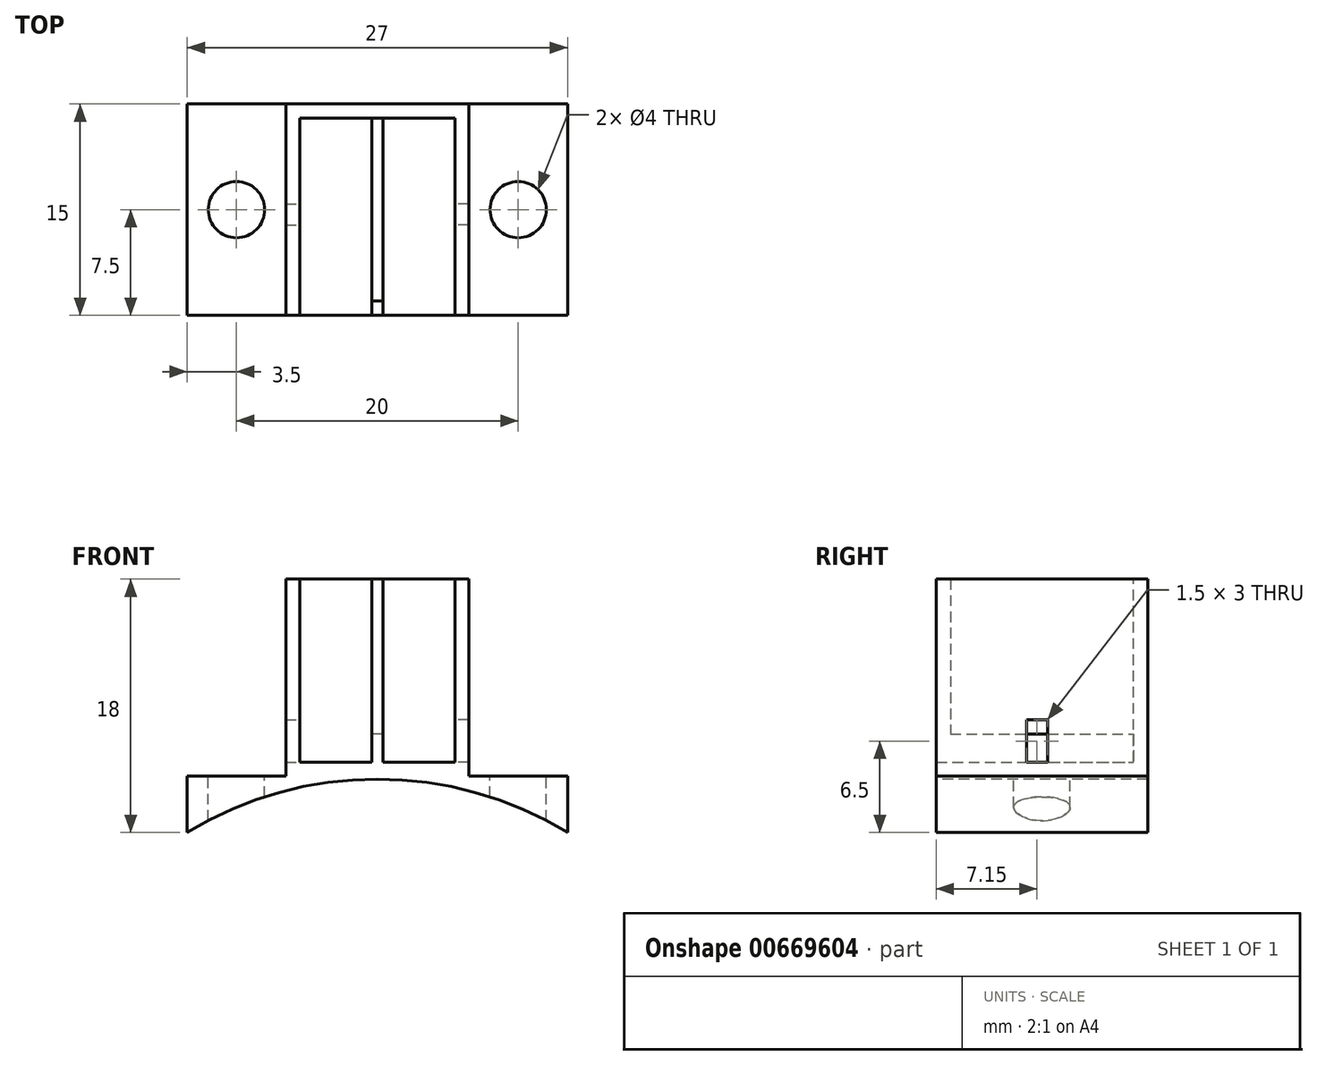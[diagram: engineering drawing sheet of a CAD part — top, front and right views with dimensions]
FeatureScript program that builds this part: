
annotation { "Feature Type Name" : "Feature", "Feature Type Description" : "" }
export const myFeature = defineFeature(function(context is Context, id is Id, definition is map)
    precondition{}
    {
        {
            var Q0;
            Q0=qCreatedBy(makeId("Top.planeOp"),FACE);
            var sketch = newSketch(context, id + "F0", { "sketchPlane" : qUnion([Q0])});
            skLineSegment(sketch, "E0.bottom", {"start": v(5.5, -6.5) * mm, "end": v(-5.5, -6.5) * mm});
            skLineSegment(sketch, "E0.top", {"start": v(5.5, 6.5) * mm, "end": v(-5.5, 6.5) * mm});
            skLineSegment(sketch, "E0.left", {"start": v(5.5, -6.5) * mm, "end": v(5.5, 6.5) * mm});
            skLineSegment(sketch, "E0.right", {"start": v(-5.5, -6.5) * mm, "end": v(-5.5, 6.5) * mm});
            skPoint(sketch, "E0.middle", {"position": v(0, 0) * mm});
            skSolve(sketch);
        }
        {
            var Q0;
            Q0=qCreatedBy(makeId("Top.planeOp"),FACE);
            var sketch = newSketch(context, id + "F1", { "sketchPlane" : qUnion([Q0])});
            skLineSegment(sketch, "E1.bottom", {"start": v(6.5, -7.5) * mm, "end": v(-6.5, -7.5) * mm});
            skLineSegment(sketch, "E1.top", {"start": v(6.5, 7.5) * mm, "end": v(-6.5, 7.5) * mm});
            skLineSegment(sketch, "E1.left", {"start": v(6.5, -7.5) * mm, "end": v(6.5, 7.5) * mm});
            skLineSegment(sketch, "E1.right", {"start": v(-6.5, -7.5) * mm, "end": v(-6.5, 7.5) * mm});
            skPoint(sketch, "E1.middle", {"position": v(0, 0) * mm});
            skSolve(sketch);
        }
        {
            var Q0;
            Q0 = qSketchRegion(id + "F1", true);
            extrude(context, id + "F2", {"entities" : qUnion([Q0]), "oppositeDirection" : true, "depth" : 18 * mm, "offsetDistance" : 25 * mm});
        }
        {
            var Q0;
            Q0 = qSketchRegion(id + "F0", true);
            extrude(context, id + "F3", {"entities" : qUnion([Q0]), "operationType" : NewBodyOperationType.REMOVE, "oppositeDirection" : true, "depth" : 13 * mm, "offsetDistance" : 25 * mm});
        }
        {
            var Q0;
            Q0=makeQuery(id+"F3.boolean.opBoolean","COPY",FACE,{"derivedFrom":makeQuery(id+"F3.opExtrude","CAP_FACE",FACE,{"disambiguationData":[OSD([sQuery(id+"F0.wireOp",EDGE,"E0.bottom"),sQuery(id+"F0.wireOp",EDGE,"E0.top"),sQuery(id+"F0.wireOp",EDGE,"E0.left"),sQuery(id+"F0.wireOp",EDGE,"E0.right")])],"isStart":false})});
            var sketch = newSketch(context, id + "F4", { "sketchPlane" : qUnion([Q0])});
            skLineSegment(sketch, "E2.bottom", {"start": v(0.4, -6.5) * mm, "end": v(-0.4, -6.5) * mm});
            skLineSegment(sketch, "E2.top", {"start": v(0.4, 6.5) * mm, "end": v(-0.4, 6.5) * mm});
            skLineSegment(sketch, "E2.left", {"start": v(0.4, -6.5) * mm, "end": v(0.4, 6.5) * mm});
            skLineSegment(sketch, "E2.right", {"start": v(-0.4, -6.5) * mm, "end": v(-0.4, 6.5) * mm});
            skPoint(sketch, "E2.middle", {"position": v(0, 0) * mm});
            skSolve(sketch);
        }
        {
            var Q0;
            Q0 = qSketchRegion(id + "F4", true);
            extrude(context, id + "F5", {"entities" : qUnion([Q0]), "operationType" : NewBodyOperationType.ADD, "depth" : 2 * mm, "offsetDistance" : 25 * mm});
        }
        {
            var Q0;
            {var subQ0=sQuery(id+"F0.wireOp",EDGE,"E0.bottom");var subQ1=sQuery(id+"F0.wireOp",EDGE,"E0.top");var subQ2=sQuery(id+"F0.wireOp",EDGE,"E0.left");Q0=makeQuery(id+"F5.boolean.opBoolean","SPLIT",FACE,{"disambiguationData":[TD([makeQuery(id+"F3.boolean.opBoolean","COPY",FACE,{"derivedFrom":makeQuery(id+"F3.opExtrude","SWEPT_FACE",FACE,{"disambiguationData":[OSD([subQ2])]})})])],"derivedFrom":makeQuery(id+"F3.boolean.opBoolean","COPY",FACE,{"derivedFrom":makeQuery(id+"F3.opExtrude","CAP_FACE",FACE,{"disambiguationData":[OSD([subQ0,subQ1,subQ2,sQuery(id+"F0.wireOp",EDGE,"E0.right")])],"isStart":false})})});}
            var sketch = newSketch(context, id + "F6", { "sketchPlane" : qUnion([Q0])});
            skLineSegment(sketch, "E3.bottom", {"start": v(0.4, -5.5) * mm, "end": v(5.5, -5.5) * mm});
            skLineSegment(sketch, "E3.top", {"start": v(0.4, -8.23) * mm, "end": v(5.5, -8.23) * mm});
            skLineSegment(sketch, "E3.left", {"start": v(0.4, -5.5) * mm, "end": v(0.4, -8.23) * mm});
            skLineSegment(sketch, "E3.right", {"start": v(5.5, -5.5) * mm, "end": v(5.5, -8.23) * mm});
            skSolve(sketch);
        }
        {
            var Q0;
            {var subQ0=sQuery(id+"F0.wireOp",EDGE,"E0.bottom");var subQ1=sQuery(id+"F0.wireOp",EDGE,"E0.top");var subQ2=sQuery(id+"F0.wireOp",EDGE,"E0.right");Q0=makeQuery(id+"F5.boolean.opBoolean","SPLIT",FACE,{"disambiguationData":[TD([makeQuery(id+"F3.boolean.opBoolean","COPY",FACE,{"derivedFrom":makeQuery(id+"F3.opExtrude","SWEPT_FACE",FACE,{"disambiguationData":[OSD([subQ2])]})})])],"derivedFrom":makeQuery(id+"F3.boolean.opBoolean","COPY",FACE,{"derivedFrom":makeQuery(id+"F3.opExtrude","CAP_FACE",FACE,{"disambiguationData":[OSD([subQ0,subQ1,sQuery(id+"F0.wireOp",EDGE,"E0.left"),subQ2])],"isStart":false})})});}
            var sketch = newSketch(context, id + "F7", { "sketchPlane" : qUnion([Q0])});
            skPoint(sketch, "E4.oppositeSnap0", {"position": v(-5.5, 0) * mm});
            skLineSegment(sketch, "E4.bottom", {"start": v(-0.44, -5.5) * mm, "end": v(-5.5, -5.5) * mm});
            skLineSegment(sketch, "E4.top", {"start": v(-0.44, -8.17) * mm, "end": v(-5.5, -8.17) * mm});
            skLineSegment(sketch, "E4.left", {"start": v(-0.44, -5.5) * mm, "end": v(-0.44, -8.17) * mm});
            skLineSegment(sketch, "E4.right", {"start": v(-5.5, -5.5) * mm, "end": v(-5.5, -8.17) * mm});
            skSolve(sketch);
        }
        {
            var Q0;
            Q0 = qSketchRegion(id + "F7", true);
            var Q1;
            Q1 = qSketchRegion(id + "F6", true);
            extrude(context, id + "F8", {"entities" : qUnion([Q0, Q1]), "operationType" : NewBodyOperationType.REMOVE, "depth" : 15 * mm, "offsetDistance" : 25 * mm});
        }
        {
            var Q0;
            Q0=makeQuery(id+"F8.boolean.opBoolean","MERGE",FACE,{"derivedFrom":[makeQuery(id+"F3.boolean.opBoolean","COPY",FACE,{"derivedFrom":makeQuery(id+"F3.opExtrude","SWEPT_FACE",FACE,{"disambiguationData":[OSD([sQuery(id+"F0.wireOp",EDGE,"E0.right")])]})}),makeQuery(id+"F8.opExtrude","SWEPT_FACE",FACE,{"disambiguationData":[OSD([sQuery(id+"F7.wireOp",EDGE,"E4.right")])]})]});
            var sketch = newSketch(context, id + "F9", { "sketchPlane" : qUnion([Q0])});
            skLineSegment(sketch, "E5.bottom", {"start": v(0.4, -10) * mm, "end": v(-1.1, -10) * mm});
            skPoint(sketch, "E5.middle", {"position": v(-0.5, -13) * mm});
            skLineSegment(sketch, "E6.top", {"start": v(0.4, -13) * mm, "end": v(-1.1, -13) * mm});
            skLineSegment(sketch, "E6.left", {"start": v(0.4, -10) * mm, "end": v(0.4, -13) * mm});
            skLineSegment(sketch, "E6.right", {"start": v(-1.1, -10) * mm, "end": v(-1.1, -13) * mm});
            skSolve(sketch);
        }
        {
            var Q0;
            Q0 = qSketchRegion(id + "F9", true);
            extrude(context, id + "F10", {"entities" : qUnion([Q0]), "operationType" : NewBodyOperationType.REMOVE, "oppositeDirection" : true, "depth" : 25 * mm, "offsetDistance" : 25 * mm});
        }
        {
            var Q0;
            Q0=makeQuery(id+"F2.opExtrude","SWEPT_BODY",BODY,{"disambiguationData":[OSD([sQuery(id+"F1.wireOp",EDGE,"E1.bottom"),sQuery(id+"F1.wireOp",EDGE,"E1.top"),sQuery(id+"F1.wireOp",EDGE,"E1.left"),sQuery(id+"F1.wireOp",EDGE,"E1.right")])]});
            var Q1;
            Q1=qCreatedBy(makeId("Right.planeOp"),FACE);
            mirror(context, id + "F11", {"operationType" : NewBodyOperationType.INTERSECT, "entities" : qUnion([Q0]), "mirrorPlane" : qUnion([Q1])});
        }
        {
            var Q0;
            Q0=makeQuery(id+"F2.opExtrude","SWEPT_FACE",FACE,{"disambiguationData":[OSD([sQuery(id+"F1.wireOp",EDGE,"E1.bottom")])]});
            var sketch = newSketch(context, id + "F12", { "sketchPlane" : qUnion([Q0])});
            skSolve(sketch);
        }
        {
            var Q0;
            Q0=makeQuery(id+"F2.opExtrude","SWEPT_FACE",FACE,{"disambiguationData":[OSD([sQuery(id+"F1.wireOp",EDGE,"E1.right")])]});
            var sketch = newSketch(context, id + "F13", { "sketchPlane" : qUnion([Q0])});
            skLineSegment(sketch, "E7.bottom", {"start": v(7.5, -18) * mm, "end": v(-7.5, -18) * mm});
            skLineSegment(sketch, "E7.top", {"start": v(7.5, -14) * mm, "end": v(-7.5, -14) * mm});
            skLineSegment(sketch, "E7.left", {"start": v(7.5, -18) * mm, "end": v(7.5, -14) * mm});
            skLineSegment(sketch, "E7.right", {"start": v(-7.5, -18) * mm, "end": v(-7.5, -14) * mm});
            skSolve(sketch);
        }
        {
            var Q0;
            Q0=makeQuery(id+"F13.imprint","IMPRINT",FACE,{"disambiguationData":[TD([[makeQuery(id+"F13.imprint","IMPRINT",EDGE,{"derivedFrom":sQuery(id+"F13.wireOp",EDGE,"E7.bottom")}),-1.0]])]});
            extrude(context, id + "F14", {"entities" : qUnion([Q0]), "operationType" : NewBodyOperationType.ADD, "depth" : 7 * mm, "offsetDistance" : 25 * mm});
        }
        {
            var Q0;
            Q0=makeQuery(id+"F14.opExtrude","SWEPT_FACE",FACE,{"disambiguationData":[OSD([sQuery(id+"F13.wireOp",EDGE,"E7.top")])]});
            var sketch = newSketch(context, id + "F15", { "sketchPlane" : qUnion([Q0])});
            skCircle(sketch, "E8", {"center": v(-10, 0) * mm, "radius": 2 * mm});
            skPoint(sketch, "E8.centerSnap0", {"position": v(-10, -7.5) * mm});
            skPoint(sketch, "E8.centerSnap1", {"position": v(-6.5, 0) * mm});
            skSolve(sketch);
        }
        {
            var Q0;
            Q0=makeQuery(id+"F15.imprint","IMPRINT",FACE,{"disambiguationData":[TD([[makeQuery(id+"F15.imprint","IMPRINT",EDGE,{"derivedFrom":sQuery(id+"F15.wireOp",EDGE,"E8")}),1.0]])]});
            extrude(context, id + "F16", {"entities" : qUnion([Q0]), "operationType" : NewBodyOperationType.REMOVE, "oppositeDirection" : true, "depth" : 25 * mm, "offsetDistance" : 25 * mm});
        }
        {
            var Q0;
            Q0=makeQuery(id+"F2.opExtrude","SWEPT_BODY",BODY,{"disambiguationData":[OSD([sQuery(id+"F1.wireOp",EDGE,"E1.bottom"),sQuery(id+"F1.wireOp",EDGE,"E1.top"),sQuery(id+"F1.wireOp",EDGE,"E1.left"),sQuery(id+"F1.wireOp",EDGE,"E1.right")])]});
            var Q1;
            Q1=qCreatedBy(makeId("Right.planeOp"),FACE);
            mirror(context, id + "F17", {"operationType" : NewBodyOperationType.ADD, "entities" : qUnion([Q0]), "mirrorPlane" : qUnion([Q1])});
        }
        {
            var Q0;
            {var subQ0=makeQuery(id+"F14.boolean.opBoolean","MERGE",FACE,{"derivedFrom":[makeQuery(id+"F2.opExtrude","SWEPT_FACE",FACE,{"disambiguationData":[OSD([sQuery(id+"F1.wireOp",EDGE,"E1.bottom")])]}),makeQuery(id+"F14.opExtrude","SWEPT_FACE",FACE,{"disambiguationData":[OSD([sQuery(id+"F13.wireOp",EDGE,"E7.left")])]})]});Q0=makeQuery(id+"F17.boolean.opBoolean","MERGE",FACE,{"derivedFrom":[subQ0,makeQuery(id+"F17.opPattern","COPY",FACE,{"derivedFrom":subQ0,"instanceName":"1"})]});}
            var sketch = newSketch(context, id + "F18", { "sketchPlane" : qUnion([Q0])});
            skArc(sketch, "E9", {"start": v(13.5, -18) * mm, "mid": v(0, -14.2) * mm, "end": v(-13.5, -18) * mm});
            skSolve(sketch);
        }
        {
            var Q0;
            Q0=makeQuery(id+"F18.imprint","IMPRINT",FACE,{"disambiguationData":[TD([[makeQuery(id+"F18.imprint","IMPRINT",EDGE,{"derivedFrom":sQuery(id+"F18.wireOp",EDGE,"E9")}),1.0]])]});
            extrude(context, id + "F19", {"entities" : qUnion([Q0]), "operationType" : NewBodyOperationType.REMOVE, "oppositeDirection" : true, "depth" : 25 * mm, "offsetDistance" : 25 * mm});
        }
    });
